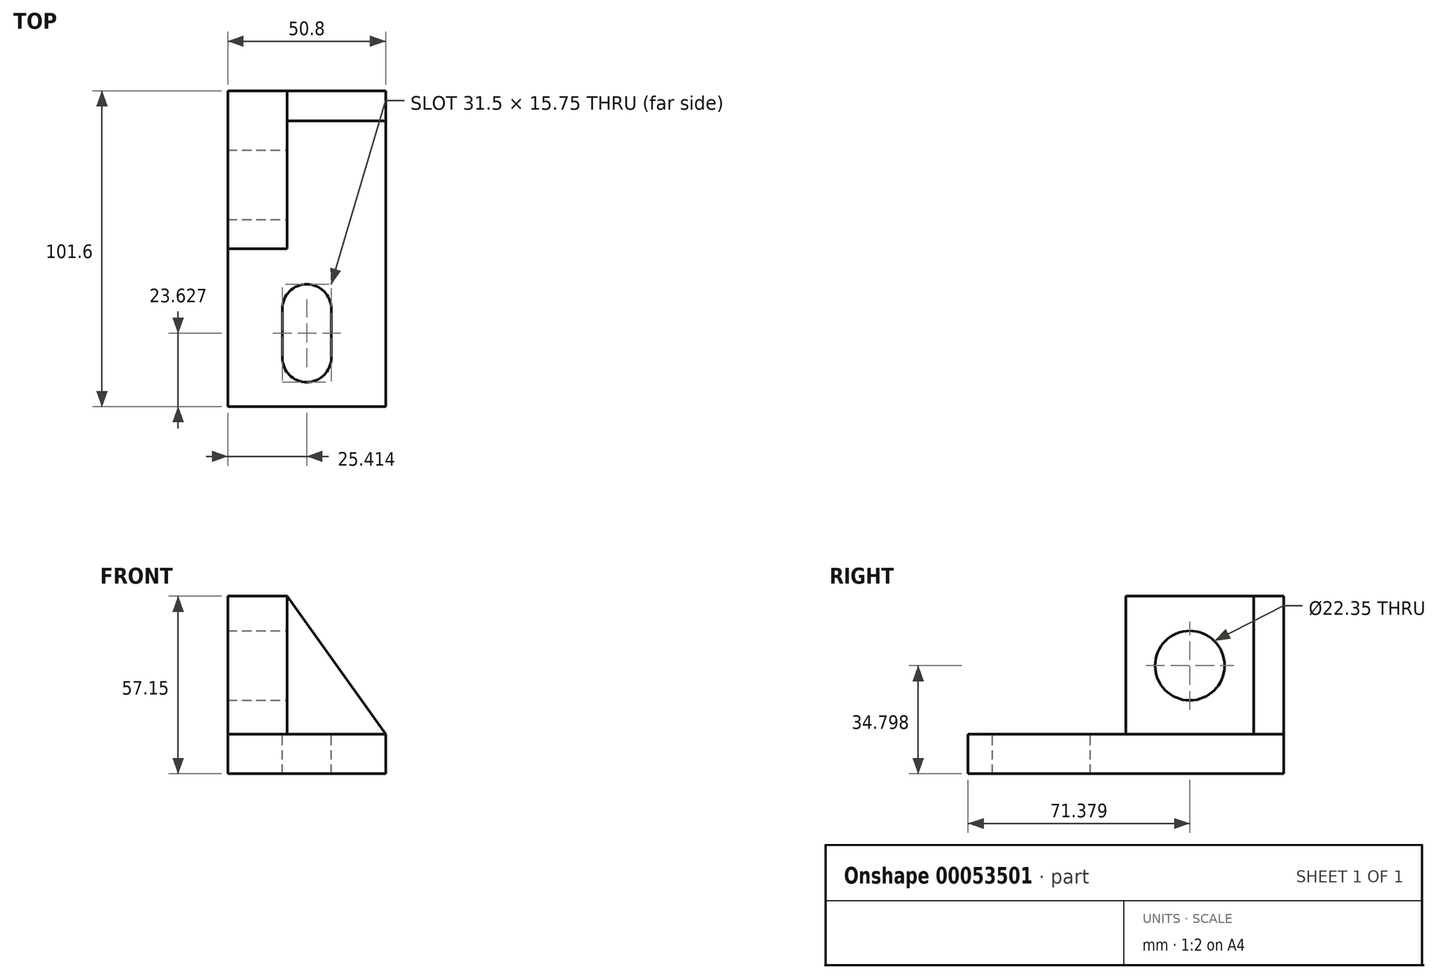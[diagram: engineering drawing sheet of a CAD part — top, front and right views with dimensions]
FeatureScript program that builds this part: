
annotation { "Feature Type Name" : "Feature", "Feature Type Description" : "" }
export const myFeature = defineFeature(function(context is Context, id is Id, definition is map)
    precondition{}
    {
        {
            var Q0;
            Q0=qCreatedBy(makeId("Top.planeOp"),FACE);
            var sketch = newSketch(context, id + "F0", { "sketchPlane" : qUnion([Q0])});
            skLineSegment(sketch, "E0.bottom", {"start": v(-19.66, 86.1) * mm, "end": v(31.14, 86.1) * mm});
            skLineSegment(sketch, "E0.top", {"start": v(-19.66, -15.5) * mm, "end": v(31.14, -15.5) * mm});
            skLineSegment(sketch, "E0.left", {"start": v(-19.66, 86.1) * mm, "end": v(-19.66, -15.5) * mm});
            skLineSegment(sketch, "E0.right", {"start": v(31.14, 86.1) * mm, "end": v(31.14, -15.5) * mm});
            skSolve(sketch);
        }
        {
            var Q0;
            Q0 = qSketchRegion(id + "F0", true);
            extrude(context, id + "F1", {"entities" : qUnion([Q0]), "depth" : 12.7 * mm});
        }
        {
            var Q0;
            Q0=makeQuery(id+"F1.opExtrude","CAP_FACE",FACE,{"disambiguationData":[OSD([sQuery(id+"F0.wireOp",EDGE,"E0.bottom"),sQuery(id+"F0.wireOp",EDGE,"E0.top"),sQuery(id+"F0.wireOp",EDGE,"E0.left"),sQuery(id+"F0.wireOp",EDGE,"E0.right")])],"isStart":false});
            var sketch = newSketch(context, id + "F2", { "sketchPlane" : qUnion([Q0])});
            skLineSegment(sketch, "E1.bottom", {"start": v(-19.66, 86.1) * mm, "end": v(-0.61, 86.1) * mm});
            skLineSegment(sketch, "E1.top", {"start": v(-19.66, 35.3) * mm, "end": v(-0.61, 35.3) * mm});
            skLineSegment(sketch, "E1.left", {"start": v(-19.66, 86.1) * mm, "end": v(-19.66, 35.3) * mm});
            skLineSegment(sketch, "E1.right", {"start": v(-0.61, 86.1) * mm, "end": v(-0.61, 35.3) * mm});
            skSolve(sketch);
        }
        {
            var Q0;
            Q0 = qSketchRegion(id + "F2", true);
            extrude(context, id + "F3", {"entities" : qUnion([Q0]), "operationType" : NewBodyOperationType.ADD, "depth" : 44.45 * mm});
        }
        {
            var Q0;
            Q0=makeQuery(id+"F1.opExtrude","CAP_FACE",FACE,{"disambiguationData":[OSD([sQuery(id+"F0.wireOp",EDGE,"E0.bottom"),sQuery(id+"F0.wireOp",EDGE,"E0.top"),sQuery(id+"F0.wireOp",EDGE,"E0.left"),sQuery(id+"F0.wireOp",EDGE,"E0.right")])],"isStart":false});
            var sketch = newSketch(context, id + "F4", { "sketchPlane" : qUnion([Q0])});
            skArc(sketch, "E2", {"start": v(-2.12, 0.25) * mm, "mid": v(5.75, -7.62) * mm, "end": v(13.63, 0.25) * mm});
            skLineSegment(sketch, "E3.left", {"start": v(13.63, 0.25) * mm, "end": v(13.63, 16) * mm});
            skLineSegment(sketch, "E3.right", {"start": v(-2.12, 0.25) * mm, "end": v(-2.12, 16) * mm});
            skArc(sketch, "E4", {"start": v(-2.12, 16) * mm, "mid": v(5.75, 23.87) * mm, "end": v(13.63, 16) * mm});
            skSolve(sketch);
        }
        {
            var Q0;
            Q0 = qSketchRegion(id + "F4", true);
            extrude(context, id + "F5", {"entities" : qUnion([Q0]), "operationType" : NewBodyOperationType.REMOVE, "oppositeDirection" : true, "depth" : 25.4 * mm});
        }
        {
            var Q0;
            Q0=makeQuery(id+"F1.opExtrude","CAP_FACE",FACE,{"disambiguationData":[OSD([sQuery(id+"F0.wireOp",EDGE,"E0.bottom"),sQuery(id+"F0.wireOp",EDGE,"E0.top"),sQuery(id+"F0.wireOp",EDGE,"E0.left"),sQuery(id+"F0.wireOp",EDGE,"E0.right")])],"isStart":false});
            var sketch = newSketch(context, id + "F6", { "sketchPlane" : qUnion([Q0])});
            skLineSegment(sketch, "E5.bottom", {"start": v(-0.61, 86.1) * mm, "end": v(31.14, 86.1) * mm});
            skLineSegment(sketch, "E5.top", {"start": v(-0.61, 76.45) * mm, "end": v(31.14, 76.45) * mm});
            skLineSegment(sketch, "E5.left", {"start": v(-0.61, 86.1) * mm, "end": v(-0.61, 76.45) * mm});
            skLineSegment(sketch, "E5.right", {"start": v(31.14, 86.1) * mm, "end": v(31.14, 76.45) * mm});
            skSolve(sketch);
        }
        {
            var Q0;
            Q0 = qSketchRegion(id + "F6", true);
            extrude(context, id + "F7", {"entities" : qUnion([Q0]), "operationType" : NewBodyOperationType.ADD, "depth" : 44.45 * mm});
        }
        {
            var Q0;
            Q0=makeQuery(id+"F7.opExtrude","CAP_EDGE",EDGE,{"disambiguationData":[OSD([sQuery(id+"F6.wireOp",EDGE,"E5.right")])],"isStart":false});
            chamfer(context, id + "F8", {"entities" : qUnion([Q0]), "chamferType" : ChamferType.OFFSET_ANGLE, "width" : 44.45 * mm, "oppositeDirection" : false, "angle" : 35.54 * degree, "tangentPropagation" : true});
        }
        {
            var Q0;
            Q0=makeQuery(id+"F3.opExtrude","SWEPT_FACE",FACE,{"disambiguationData":[OSD([sQuery(id+"F2.wireOp",EDGE,"E1.right")])]});
            var sketch = newSketch(context, id + "F9", { "sketchPlane" : qUnion([Q0])});
            skCircle(sketch, "E6", {"center": v(55.88, 34.8) * mm, "radius": 11.18 * mm});
            skSolve(sketch);
        }
        {
            var Q0;
            Q0=makeQuery(id+"F9.imprint","IMPRINT",FACE,{"disambiguationData":[TD([[makeQuery(id+"F9.imprint","IMPRINT",EDGE,{"derivedFrom":sQuery(id+"F9.wireOp",EDGE,"E6")}),1.0]])]});
            var Q1;
            Q1=sQuery(id+"F9.wireOp",EDGE,"E6");
            extrude(context, id + "F10", {"entities" : qUnion([Q0]), "operationType" : NewBodyOperationType.REMOVE, "surfaceEntities" : qUnion([Q1]), "oppositeDirection" : true, "depth" : 25.4 * mm});
        }
    });
